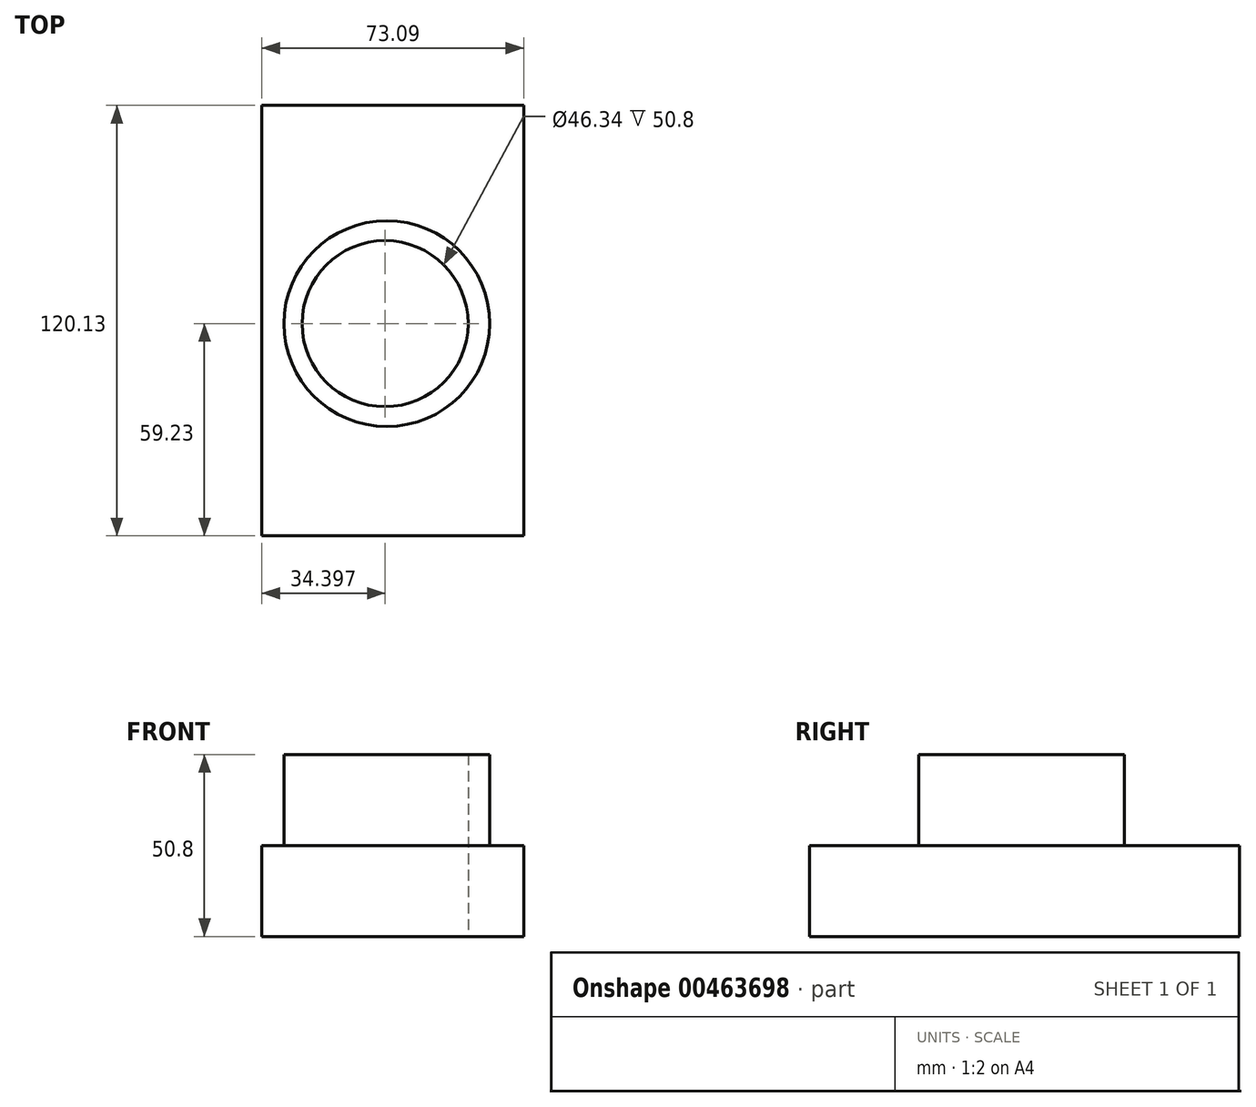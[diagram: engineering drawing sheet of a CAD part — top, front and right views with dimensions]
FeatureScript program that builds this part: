
annotation { "Feature Type Name" : "Feature", "Feature Type Description" : "" }
export const myFeature = defineFeature(function(context is Context, id is Id, definition is map)
    precondition{}
    {
        {
            var Q0;
            Q0=qCreatedBy(makeId("Top.planeOp"),FACE);
            var sketch = newSketch(context, id + "F0", { "sketchPlane" : qUnion([Q0])});
            skLineSegment(sketch, "E0.bottom", {"start": v(-54.22, 60.9) * mm, "end": v(18.87, 60.9) * mm});
            skLineSegment(sketch, "E0.top", {"start": v(-54.22, -59.23) * mm, "end": v(18.87, -59.23) * mm});
            skLineSegment(sketch, "E0.left", {"start": v(-54.22, 60.9) * mm, "end": v(-54.22, -59.23) * mm});
            skLineSegment(sketch, "E0.right", {"start": v(18.87, 60.9) * mm, "end": v(18.87, -59.23) * mm});
            skSolve(sketch);
        }
        {
            var Q0;
            Q0=qCreatedBy(makeId("Top.planeOp"),FACE);
            var sketch = newSketch(context, id + "F1", { "sketchPlane" : qUnion([Q0])});
            skCircle(sketch, "E1", {"center": v(-19.35, 0) * mm, "radius": 28.71 * mm});
            skSolve(sketch);
        }
        {
            var Q0;
            Q0 = qSketchRegion(id + "F1", true);
            extrude(context, id + "F2", {"entities" : qUnion([Q0]), "depth" : 50.8 * mm});
        }
        {
            var Q0;
            Q0=makeQuery(id+"F0.imprint","IMPRINT",FACE,{"disambiguationData":[TD([[makeQuery(id+"F0.imprint","IMPRINT",EDGE,{"derivedFrom":sQuery(id+"F0.wireOp",EDGE,"E0.bottom")}),-1.0]])]});
            extrude(context, id + "F3", {"entities" : qUnion([Q0]), "operationType" : NewBodyOperationType.ADD, "depth" : 25.4 * mm});
        }
        {
            var Q0;
            Q0=qCreatedBy(makeId("Top.planeOp"),FACE);
            var sketch = newSketch(context, id + "F4", { "sketchPlane" : qUnion([Q0])});
            skCircle(sketch, "E2", {"center": v(-19.82, 0) * mm, "radius": 23.17 * mm});
            skSolve(sketch);
        }
        {
            var Q0;
            Q0 = qSketchRegion(id + "F4", true);
            var Q1;
            Q1 = qConstructionFilter(qBodyType(qCreatedBy(id + "F4" ,EDGE), BodyType.WIRE), ConstructionObject.NO);
            extrude(context, id + "F5", {"entities" : qUnion([Q0]), "operationType" : NewBodyOperationType.REMOVE, "surfaceEntities" : qUnion([Q1]), "depth" : 149.1 * mm});
        }
        {
            var Q0;
            Q0=makeQuery(id+"F4.imprint","IMPRINT",FACE,{"disambiguationData":[TD([[makeQuery(id+"F4.imprint","IMPRINT",EDGE,{"derivedFrom":sQuery(id+"F4.wireOp",EDGE,"E2")}),1.0]])]});
            extrude(context, id + "F6", {"entities" : qUnion([Q0]), "operationType" : NewBodyOperationType.REMOVE, "depth" : 50.8 * mm});
        }
    });
